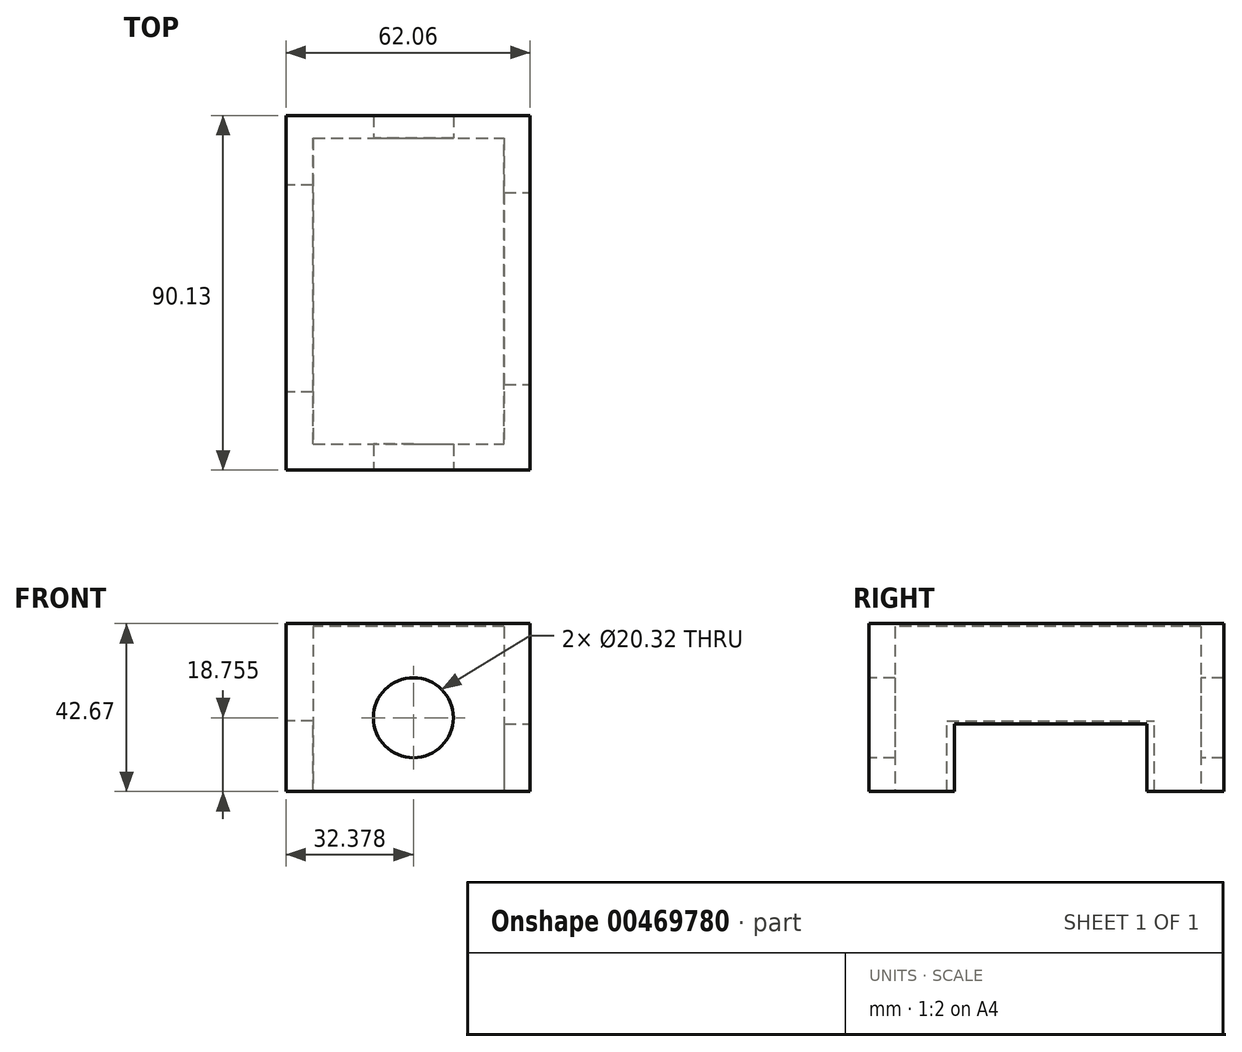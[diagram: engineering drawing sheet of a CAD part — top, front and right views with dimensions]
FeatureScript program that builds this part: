
annotation { "Feature Type Name" : "Feature", "Feature Type Description" : "" }
export const myFeature = defineFeature(function(context is Context, id is Id, definition is map)
    precondition{}
    {
        {
            var Q0;
            Q0=qCreatedBy(makeId("Top.planeOp"),FACE);
            var sketch = newSketch(context, id + "F0", { "sketchPlane" : qUnion([Q0])});
            skLineSegment(sketch, "E0.bottom", {"start": v(-28.06, 44.12) * mm, "end": v(34, 44.12) * mm});
            skLineSegment(sketch, "E0.top", {"start": v(-28.06, -46) * mm, "end": v(34, -46) * mm});
            skLineSegment(sketch, "E0.left", {"start": v(-28.06, 44.12) * mm, "end": v(-28.06, -46) * mm});
            skLineSegment(sketch, "E0.right", {"start": v(34, 44.12) * mm, "end": v(34, -46) * mm});
            skSolve(sketch);
        }
        {
            var Q0;
            Q0=makeQuery(id+"F0.imprint","IMPRINT",FACE,{"disambiguationData":[TD([[makeQuery(id+"F0.imprint","IMPRINT",EDGE,{"derivedFrom":sQuery(id+"F0.wireOp",EDGE,"E0.bottom")}),-1.0]])]});
            extrude(context, id + "F1", {"entities" : qUnion([Q0]), "depth" : 42.67 * mm});
        }
        {
            var Q0;
            Q0=qCreatedBy(makeId("Top.planeOp"),FACE);
            var sketch = newSketch(context, id + "F2", { "sketchPlane" : qUnion([Q0])});
            skLineSegment(sketch, "E1.bottom", {"start": v(-21.18, -39.4) * mm, "end": v(27.39, -39.4) * mm});
            skLineSegment(sketch, "E1.top", {"start": v(-21.18, 38.32) * mm, "end": v(27.39, 38.32) * mm});
            skLineSegment(sketch, "E1.left", {"start": v(-21.18, -39.4) * mm, "end": v(-21.18, 38.32) * mm});
            skLineSegment(sketch, "E1.right", {"start": v(27.39, -39.4) * mm, "end": v(27.39, 38.32) * mm});
            skSolve(sketch);
        }
        {
            var Q0;
            Q0=makeQuery(id+"F2.imprint","IMPRINT",FACE,{"disambiguationData":[TD([[makeQuery(id+"F2.imprint","IMPRINT",EDGE,{"derivedFrom":sQuery(id+"F2.wireOp",EDGE,"E1.bottom")}),1.0]])]});
            extrude(context, id + "F3", {"entities" : qUnion([Q0]), "operationType" : NewBodyOperationType.REMOVE, "depth" : 76.45 * mm});
        }
        {
            var Q0;
            Q0=makeQuery(id+"F1.opExtrude","CAP_FACE",FACE,{"disambiguationData":[OSD([sQuery(id+"F0.wireOp",EDGE,"E0.bottom"),sQuery(id+"F0.wireOp",EDGE,"E0.top"),sQuery(id+"F0.wireOp",EDGE,"E0.left"),sQuery(id+"F0.wireOp",EDGE,"E0.right")])],"isStart":false});
            var sketch = newSketch(context, id + "F4", { "sketchPlane" : qUnion([Q0])});
            skLineSegment(sketch, "E2.bottom", {"start": v(-21.18, 38.32) * mm, "end": v(27.39, 38.32) * mm});
            skLineSegment(sketch, "E2.top", {"start": v(-21.18, -39.4) * mm, "end": v(27.39, -39.4) * mm});
            skLineSegment(sketch, "E2.left", {"start": v(-21.18, 38.32) * mm, "end": v(-21.18, -39.4) * mm});
            skLineSegment(sketch, "E2.right", {"start": v(27.39, 38.32) * mm, "end": v(27.39, -39.4) * mm});
            skSolve(sketch);
        }
        {
            var Q0;
            Q0=makeQuery(id+"F4.imprint","IMPRINT",FACE,{"disambiguationData":[TD([[makeQuery(id+"F4.imprint","IMPRINT",EDGE,{"derivedFrom":sQuery(id+"F4.wireOp",EDGE,"E2.bottom")}),1.0]])]});
            extrude(context, id + "F5", {"entities" : qUnion([Q0]), "operationType" : NewBodyOperationType.ADD, "oppositeDirection" : true, "depth" : 0.76 * mm});
        }
        {
            var Q0;
            Q0=makeQuery(id+"F1.opExtrude","SWEPT_FACE",FACE,{"disambiguationData":[OSD([sQuery(id+"F0.wireOp",EDGE,"E0.top")])]});
            var sketch = newSketch(context, id + "F6", { "sketchPlane" : qUnion([Q0])});
            skCircle(sketch, "E3", {"center": v(4.32, 18.75) * mm, "radius": 8.84 * mm});
            skSolve(sketch);
        }
        {
            var Q0;
            Q0=sQuery(id+"F6.wireOp",VERTEX,"E3.center");
            var Q1;
            Q1=makeQuery(id+"F1.opExtrude","SWEPT_BODY",BODY,{"disambiguationData":[OSD([sQuery(id+"F0.wireOp",EDGE,"E0.bottom"),sQuery(id+"F0.wireOp",EDGE,"E0.top"),sQuery(id+"F0.wireOp",EDGE,"E0.left"),sQuery(id+"F0.wireOp",EDGE,"E0.right")])]});
            hole(context, id + "F7", {"style" : HoleStyle.SIMPLE, "endStyle" : HoleEndStyle.THROUGH, "holeDiameter" : 20.32 * mm, "isTappedThrough" : true, "tappedDepth" : 12.7 * mm, "tapClearance" : 3, "locations" : qUnion([Q0]), "scope" : qUnion([Q1])});
        }
        {
            var Q0;
            Q0=makeQuery(id+"F1.opExtrude","SWEPT_FACE",FACE,{"disambiguationData":[OSD([sQuery(id+"F0.wireOp",EDGE,"E0.right")])]});
            var sketch = newSketch(context, id + "F8", { "sketchPlane" : qUnion([Q0])});
            skLineSegment(sketch, "E4.bottom", {"start": v(24.02, 0) * mm, "end": v(-28.87, 0) * mm});
            skLineSegment(sketch, "E4.top", {"start": v(24.02, 23.07) * mm, "end": v(-28.87, 23.07) * mm});
            skLineSegment(sketch, "E4.left", {"start": v(24.02, 0) * mm, "end": v(24.02, 23.07) * mm});
            skLineSegment(sketch, "E4.right", {"start": v(-28.87, 0) * mm, "end": v(-28.87, 23.07) * mm});
            skSolve(sketch);
        }
        {
            var Q0;
            Q0=makeQuery(id+"F8.imprint","IMPRINT",FACE,{"disambiguationData":[TD([[makeQuery(id+"F8.imprint","IMPRINT",EDGE,{"derivedFrom":sQuery(id+"F8.wireOp",EDGE,"E4.bottom")}),-1.0]])]});
            extrude(context, id + "F9", {"entities" : qUnion([Q0]), "operationType" : NewBodyOperationType.REMOVE, "depth" : 43.69 * mm});
        }
        {
            var Q0;
            Q0=makeQuery(id+"F1.opExtrude","SWEPT_FACE",FACE,{"disambiguationData":[OSD([sQuery(id+"F0.wireOp",EDGE,"E0.left")])]});
            var sketch = newSketch(context, id + "F10", { "sketchPlane" : qUnion([Q0])});
            skLineSegment(sketch, "E5.bottom", {"start": v(26.18, 0) * mm, "end": v(-26.45, 0) * mm});
            skLineSegment(sketch, "E5.top", {"start": v(26.18, 17.94) * mm, "end": v(-26.45, 17.94) * mm});
            skLineSegment(sketch, "E5.left", {"start": v(26.18, 0) * mm, "end": v(26.18, 17.94) * mm});
            skLineSegment(sketch, "E5.right", {"start": v(-26.45, 0) * mm, "end": v(-26.45, 17.94) * mm});
            skSolve(sketch);
        }
        {
            var Q0;
            Q0=makeQuery(id+"F10.imprint","IMPRINT",FACE,{"disambiguationData":[TD([[makeQuery(id+"F10.imprint","IMPRINT",EDGE,{"derivedFrom":sQuery(id+"F10.wireOp",EDGE,"E5.bottom")}),1.0]])]});
            var sketch = newSketch(context, id + "F11", { "sketchPlane" : qUnion([Q0])});
            skSolve(sketch);
        }
        {
            var Q0;
            Q0 = qSketchRegion(id + "F11", true);
            var Q1;
            Q1=makeQuery(id+"F10.imprint","IMPRINT",FACE,{"disambiguationData":[TD([[makeQuery(id+"F10.imprint","IMPRINT",EDGE,{"derivedFrom":sQuery(id+"F10.wireOp",EDGE,"E5.bottom")}),1.0]])]});
            extrude(context, id + "F12", {"entities" : qUnion([Q0, Q1]), "operationType" : NewBodyOperationType.REMOVE, "oppositeDirection" : true, "depth" : 25.4 * mm});
        }
        {
            var Q0;
            Q0=makeQuery(id+"F1.opExtrude","SWEPT_FACE",FACE,{"disambiguationData":[OSD([sQuery(id+"F0.wireOp",EDGE,"E0.right")])]});
            var sketch = newSketch(context, id + "F13", { "sketchPlane" : qUnion([Q0])});
            skLineSegment(sketch, "E6.bottom", {"start": v(24.56, 0) * mm, "end": v(-24.29, 0) * mm});
            skLineSegment(sketch, "E6.top", {"start": v(24.56, 17.14) * mm, "end": v(-24.29, 17.14) * mm});
            skLineSegment(sketch, "E6.left", {"start": v(24.56, 0) * mm, "end": v(24.56, 17.14) * mm});
            skLineSegment(sketch, "E6.right", {"start": v(-24.29, 0) * mm, "end": v(-24.29, 17.14) * mm});
            skSolve(sketch);
        }
        {
            var Q0;
            Q0=makeQuery(id+"F13.imprint","IMPRINT",FACE,{"disambiguationData":[TD([[makeQuery(id+"F13.imprint","IMPRINT",EDGE,{"derivedFrom":sQuery(id+"F13.wireOp",EDGE,"E6.bottom")}),-1.0]])]});
            extrude(context, id + "F14", {"entities" : qUnion([Q0]), "operationType" : NewBodyOperationType.REMOVE, "oppositeDirection" : true, "depth" : 25.4 * mm});
        }
    });
